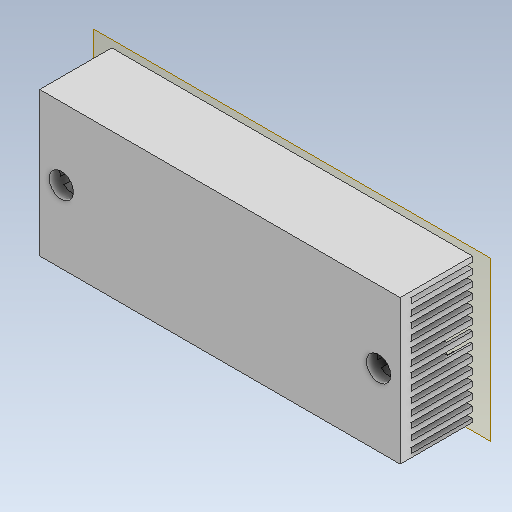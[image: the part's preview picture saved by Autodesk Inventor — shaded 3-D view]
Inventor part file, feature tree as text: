
AUTODESK INVENTOR PART (.ipt)
format: ipt  version: 2021 (Build 250183000, 183)  size: 235,520 bytes
history: native  units: in
note: dims shown in document units (in); Inventor stores cm internally (conversion verified against a paired STEP export)
features: other x3, sketch x3, plane x1
ambient origin geometry x8: Origin, YZ Plane, XZ Plane, XY Plane, X Axis, Y Axis, Z Axis, Center Point
bodies: Solid1 (feature_tree)
feature tree (7):
  other  "ExternalHeatSinkandClamp.ipt"
  other  "Solid1::ExternalHeatSinkandClamp.ipt"
  other  "TaggingFeature1"
  sketch  "Sketch1"  dims[d0=0.3937in]
  sketch  "Sketch2"  dims[d1=0.12in]
  sketch  "Sketch4"
  plane  "Work Plane1"
